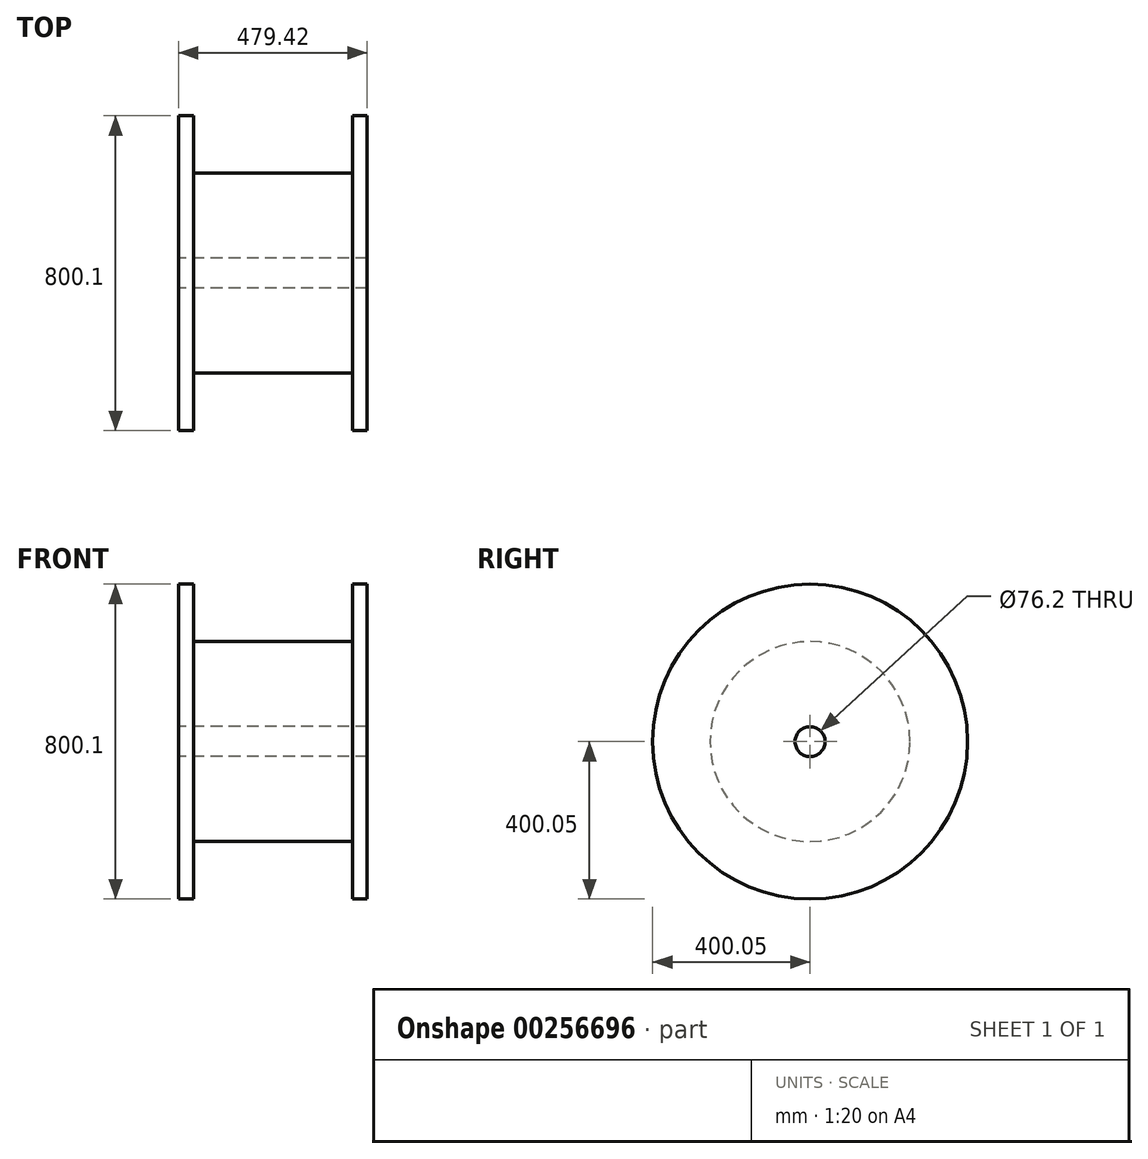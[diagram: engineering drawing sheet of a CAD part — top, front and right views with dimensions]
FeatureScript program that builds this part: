
annotation { "Feature Type Name" : "Feature", "Feature Type Description" : "" }
export const myFeature = defineFeature(function(context is Context, id is Id, definition is map)
    precondition{}
    {
        {
            var Q0;
            Q0=qCreatedBy(makeId("Top.planeOp"),FACE);
            var sketch = newSketch(context, id + "F0", { "sketchPlane" : qUnion([Q0])});
            skLineSegment(sketch, "E0", {"start": v(-220.66, -400.05) * mm, "end": v(-182.56, -400.05) * mm});
            skLineSegment(sketch, "E1", {"start": v(-182.56, -400.05) * mm, "end": v(-182.56, -254) * mm});
            skLineSegment(sketch, "E2", {"start": v(-182.56, -254) * mm, "end": v(220.66, -254) * mm});
            skLineSegment(sketch, "E3", {"start": v(220.66, -254) * mm, "end": v(220.66, -400.05) * mm});
            skLineSegment(sketch, "E4", {"start": v(220.66, -400.05) * mm, "end": v(258.76, -400.05) * mm});
            skLineSegment(sketch, "E5", {"start": v(-220.66, -400.05) * mm, "end": v(-220.66, -38.1) * mm});
            skLineSegment(sketch, "E6", {"start": v(-220.66, -38.1) * mm, "end": v(258.76, -38.1) * mm});
            skLineSegment(sketch, "E7", {"start": v(258.76, -38.1) * mm, "end": v(258.76, -400.05) * mm});
            skLineSegment(sketch, "E8", {"start": v(-266.43, 0) * mm, "end": v(267.9, 0) * mm, "construction": true});
            skSolve(sketch);
        }
        {
            var Q0;
            Q0=makeQuery(id+"F0.imprint","IMPRINT",FACE,{"disambiguationData":[TD([[makeQuery(id+"F0.imprint","IMPRINT",EDGE,{"derivedFrom":sQuery(id+"F0.wireOp",EDGE,"E0")}),1.0]])]});
            var Q1;
            Q1=sQuery(id+"F0.wireOp",EDGE,"E8");
            revolve(context, id + "F1", {"entities" : qUnion([Q0]), "axis" : qUnion([Q1]), "revolveType" : RevolveType.FULL});
        }
    });
